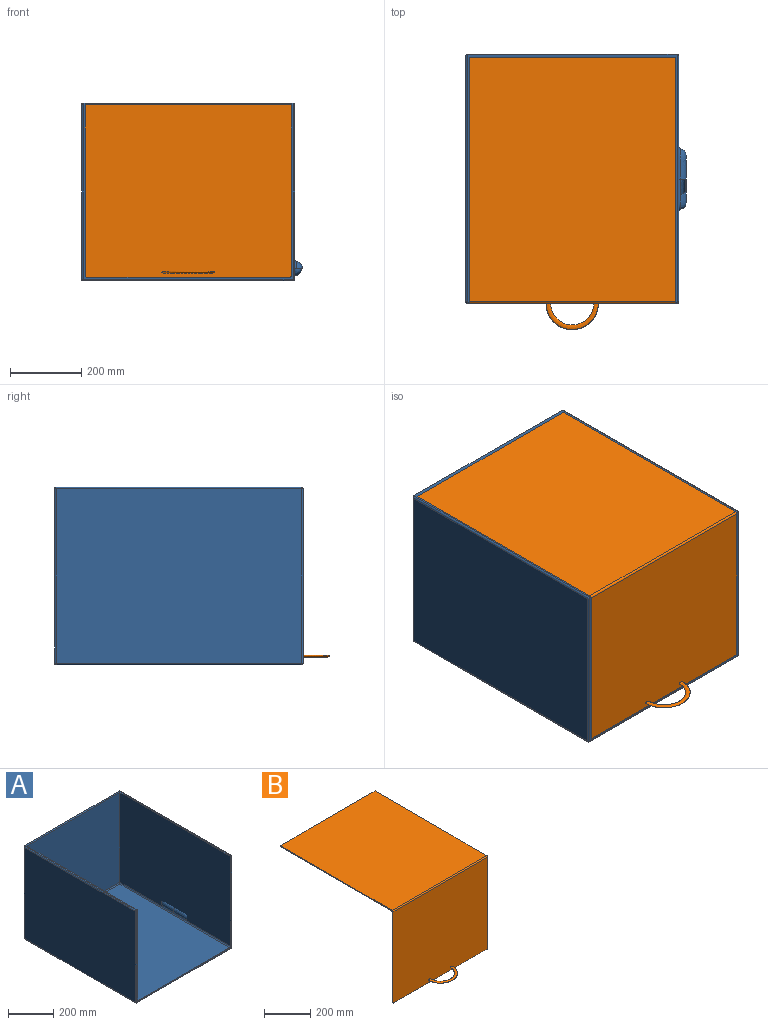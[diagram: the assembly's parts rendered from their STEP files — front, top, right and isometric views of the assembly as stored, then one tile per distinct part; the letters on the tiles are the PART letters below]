
ASSEMBLY  parts=2 mates=1
PART A: 38 faces, bbox 626.9x704.3x504.3 mm
  f0: plane 690x490mm, normal (1,0,0), area 336572.4mm2, adj f22,f25,f26,f30,f31,f32,f35,f36
  f1: plane 590x490mm, normal (0,-1,0), area 7810.7mm2, adj f6,f8,f9,f10,f11,f12,f14,f21
  f2: plane 590x495mm, normal (0,1,0), area 292050mm2, adj f4,f15,f19,f22
  f3: plane 690x490mm, normal (-1,0,0), area 338100mm2, adj f15,f16,f20,f21
  f4: plane 695x590mm, normal (0,0,1), area 12750mm2, adj f2,f6,f7,f8,f10,f11,f16,f25
  f5: plane 690x590mm, normal (0,0,-1), area 407100mm2, adj f19,f20,f26,f27
  f6: plane 690x485mm, normal (-1,0,0), area 334644.6mm2, adj f1,f4,f7,f11,f12
  f7: plane 580x485mm, normal (0,-1,0), area 281300mm2, adj f4,f6,f8,f13
  f8: plane 690x485mm, normal (1,0,0), area 334644.6mm2, adj f1,f4,f7,f10,f14
  f9: plane 685x570mm, normal (0,0,1), area 390450mm2, adj f1,f12,f13,f14
  f10: cylinder r=5mm len=5mm, axis (-1,0,0), area 39.3mm2, adj f1,f4,f8,f18
  f11: cylinder r=5mm len=5mm, axis (-1,0,0), area 39.3mm2, adj f1,f4,f6,f28
  f12: cylinder r=5mm len=690mm, axis (0,-1,0), area 5399.6mm2, adj f1,f6,f9,f13
  f13: cylinder r=5mm len=580mm, axis (1,0,0), area 4516mm2, adj f7,f9,f12,f14
  f14: cylinder r=5mm len=690mm, axis (0,1,0), area 5399.6mm2, adj f1,f8,f9,f13
  f15: cylinder r=5mm len=495mm, axis (0,0,1), area 3868.1mm2, adj f2,f3,f16,f17
  f16: cylinder r=5mm len=695mm, axis (0,1,0), area 5438.9mm2, adj f3,f4,f15,f18
  f17: sphere r=5mm, area 53.5mm2, adj f15,f19,f20
  f18: sphere r=5mm, area 25mm2, adj f10,f16,f21
  f19: cylinder r=5mm len=590mm, axis (-1,0,0), area 4633.8mm2, adj f2,f5,f17,f23
  f20: cylinder r=5mm len=690mm, axis (0,-1,0), area 5419.2mm2, adj f3,f5,f17,f24
  f21: cylinder r=5mm len=490mm, axis (0,0,-1), area 3848.5mm2, adj f1,f3,f18,f24
  f22: cylinder r=5mm len=495mm, axis (0,0,-1), area 3868.1mm2, adj f0,f2,f23,f25
  f23: sphere r=5mm, area 25mm2, adj f19,f22,f26
  f24: sphere r=5mm, area 25mm2, adj f20,f21,f27
  f25: cylinder r=5mm len=695mm, axis (0,-1,0), area 5438.9mm2, adj f0,f4,f22,f28
  f26: cylinder r=5mm len=690mm, axis (0,1,0), area 5419.2mm2, adj f0,f5,f23,f29
  f27: cylinder r=5mm len=590mm, axis (1,0,0), area 4633.8mm2, adj f1,f5,f24,f29
  f28: sphere r=5mm, area 25mm2, adj f11,f25,f30
  f29: sphere r=5mm, area 53.5mm2, adj f26,f27,f30
  f30: cylinder r=5mm len=490mm, axis (0,0,1), area 3848.5mm2, adj f0,f1,f28,f29
  f31: revolved ~83.73x18.57mm, area 2240.3mm2, adj f0,f32,f35
  f32: revolved ~83.73x18.57mm, area 2131.5mm2, adj f0,f31,f35
  f33: revolved ~85.98x21.08mm, area 2351mm2, adj f34,f35,f36
  f34: revolved ~85.98x21.08mm, area 2351mm2, adj f33,f35,f37
  f35: plane 185.77x26.85mm, normal (0.09,0,-1), area 617.6mm2, adj f0,f31,f32,f33,f34,f36,f37
  f36: bspline ~94.88x27.01mm, area 690.5mm2, adj f0,f33,f35,f37
  f37: bspline ~94.89x28.04mm, area 690.5mm2, adj f0,f34,f35,f36
PART B: 13 faces, bbox 580x763.7x490 mm
  f0: plane 580x485mm, normal (0,-1,0), area 281187.3mm2, adj f2,f3,f7,f8,f9,f11,f12
  f1: plane 680x580mm, normal (0,0,-1), area 394400mm2, adj f2,f3,f5,f10
  f2: plane 690x485mm, normal (-1,0,0), area 5850mm2, adj f0,f1,f4,f5,f6,f8,f10,f12
  f3: plane 690x485mm, normal (1,0,0), area 5850mm2, adj f0,f1,f4,f5,f6,f8,f10,f11
  f4: plane 685x580mm, normal (0,0,1), area 397300mm2, adj f2,f3,f5,f8
  f5: plane 580x5mm, normal (0,1,0), area 2900mm2, adj f1,f2,f3,f4
  f6: plane 580x480mm, normal (0,1,0), area 278389.3mm2, adj f2,f3,f7,f10,f11,f12
  f7: plane 570x5mm, normal (0,0,-1), area 2850mm2, adj f0,f6,f11,f12
  f8: cylinder r=5mm len=580mm, axis (1,0,0), area 4555.3mm2, adj f0,f2,f3,f4
  f9: revolved ~147.32x73.66mm, area 6305.7mm2, adj f0
  f10: cylinder r=5mm len=580mm, axis (-1,0,0), area 4555.3mm2, adj f1,f2,f3,f6
  f11: cylinder r=5mm len=5mm, axis (0,1,0), area 39.3mm2, adj f0,f3,f6,f7
  f12: cylinder r=5mm len=5mm, axis (0,-1,0), area 39.3mm2, adj f0,f2,f6,f7
PLACE A at identity
PLACE B at identity
MATE revolute B.f2 <-> A.f8  axis (-1,0,0) through (-290,340,500)mm
